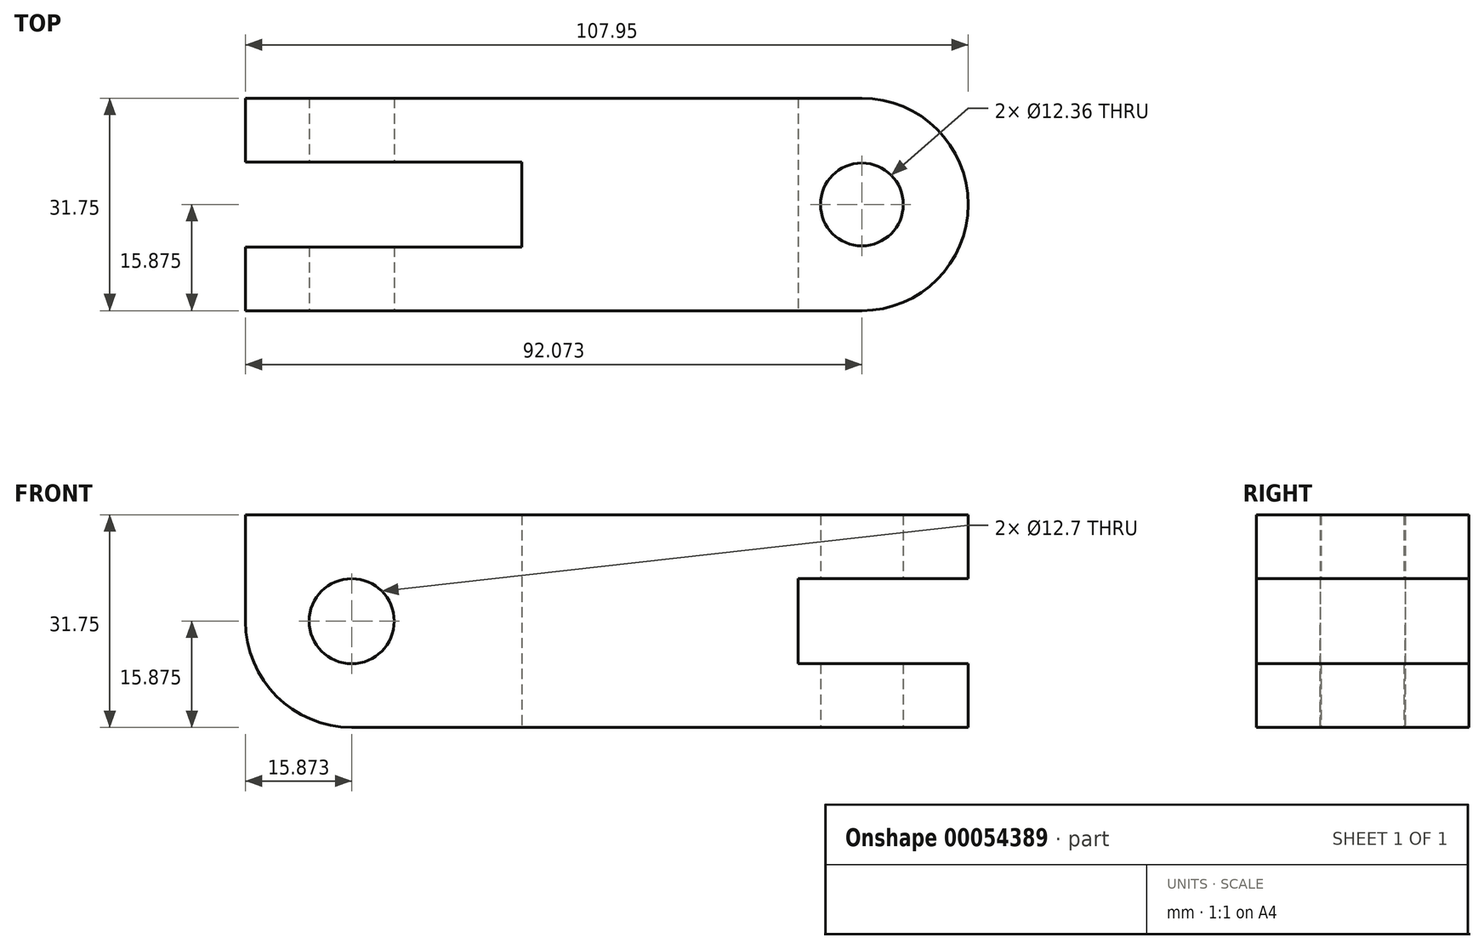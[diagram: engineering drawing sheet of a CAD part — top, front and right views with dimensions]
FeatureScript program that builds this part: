
annotation { "Feature Type Name" : "Feature", "Feature Type Description" : "" }
export const myFeature = defineFeature(function(context is Context, id is Id, definition is map)
    precondition{}
    {
        {
            var Q0;
            Q0=qCreatedBy(makeId("Top.planeOp"),FACE);
            var sketch = newSketch(context, id + "F0", { "sketchPlane" : qUnion([Q0])});
            skLineSegment(sketch, "E0.bottom", {"start": v(-48.28, -15.84) * mm, "end": v(43.8, -15.84) * mm});
            skLineSegment(sketch, "E0.top", {"start": v(-48.28, -47.59) * mm, "end": v(43.8, -47.59) * mm});
            skLineSegment(sketch, "E0.left", {"start": v(-48.28, -15.84) * mm, "end": v(-48.28, -25.36) * mm});
            skLineSegment(sketch, "E1", {"start": v(-48.28, -25.36) * mm, "end": v(-7, -25.36) * mm});
            skLineSegment(sketch, "E2", {"start": v(-48.28, -38.06) * mm, "end": v(-7, -38.06) * mm});
            skLineSegment(sketch, "E3", {"start": v(43.8, -15.84) * mm, "end": v(43.8, -15.84) * mm});
            skLineSegment(sketch, "E4", {"start": v(-7, -25.36) * mm, "end": v(-7, -38.06) * mm});
            skCircle(sketch, "E5", {"center": v(43.8, -31.71) * mm, "radius": 6.18 * mm});
            skArc(sketch, "E6", {"start": v(43.8, -47.59) * mm, "mid": v(59.67, -31.71) * mm, "end": v(43.8, -15.84) * mm});
            skLineSegment(sketch, "E7.trimOffspring", {"start": v(43.8, -47.59) * mm, "end": v(43.8, -47.59) * mm});
            skLineSegment(sketch, "E8.trimOffspring", {"start": v(-48.28, -38.06) * mm, "end": v(-48.28, -47.59) * mm});
            skSolve(sketch);
        }
        {
            var Q0;
            Q0 = qSketchRegion(id + "F0", true);
            extrude(context, id + "F1", {"entities" : qUnion([Q0]), "depth" : 31.75 * mm});
        }
        {
            var Q0;
            Q0=makeQuery(id+"F1.opExtrude","SWEPT_FACE",FACE,{"disambiguationData":[OSD([sQuery(id+"F0.wireOp",EDGE,"E0.top")])]});
            var sketch = newSketch(context, id + "F2", { "sketchPlane" : qUnion([Q0])});
            skLineSegment(sketch, "E9.bottom", {"start": v(-32.4, 31.75) * mm, "end": v(59.67, 31.75) * mm});
            skLineSegment(sketch, "E9.top", {"start": v(-32.4, 0) * mm, "end": v(59.67, 0) * mm});
            skLineSegment(sketch, "E9.right", {"start": v(59.67, 31.75) * mm, "end": v(59.67, 22.23) * mm});
            skLineSegment(sketch, "E10", {"start": v(34.27, 22.23) * mm, "end": v(34.27, 9.52) * mm});
            skArc(sketch, "E11", {"start": v(-32.4, 31.75) * mm, "mid": v(-48.28, 15.87) * mm, "end": v(-32.4, 0) * mm});
            skLineSegment(sketch, "E12", {"start": v(59.67, 22.23) * mm, "end": v(34.27, 22.23) * mm});
            skLineSegment(sketch, "E13", {"start": v(34.27, 9.52) * mm, "end": v(59.67, 9.52) * mm});
            skCircle(sketch, "E14", {"center": v(-32.4, 15.87) * mm, "radius": 6.35 * mm});
            skLineSegment(sketch, "E15.trimOffspring", {"start": v(59.67, 9.52) * mm, "end": v(59.67, 0) * mm});
            skLineSegment(sketch, "E16.bottom", {"start": v(34.27, 22.23) * mm, "end": v(59.67, 22.23) * mm});
            skLineSegment(sketch, "E16.right", {"start": v(59.67, 22.23) * mm, "end": v(59.67, 9.52) * mm});
            skLineSegment(sketch, "E17", {"start": v(-48.28, 31.75) * mm, "end": v(-48.28, 0) * mm});
            skLineSegment(sketch, "E18", {"start": v(-32.4, 31.75) * mm, "end": v(-48.28, 31.75) * mm});
            skLineSegment(sketch, "E19.bottom", {"start": v(-48.28, 31.75) * mm, "end": v(-32.4, 31.75) * mm});
            skLineSegment(sketch, "E19.top", {"start": v(-48.28, 0) * mm, "end": v(-32.4, 0) * mm});
            skLineSegment(sketch, "E19.right", {"start": v(-32.4, 31.75) * mm, "end": v(-32.4, 0) * mm});
            skSolve(sketch);
        }
        {
            var Q0;
            Q0=makeQuery(id+"F2.imprint","IMPRINT",FACE,{"disambiguationData":[TD([[makeQuery(id+"F2.imprint","IMPRINT",EDGE,{"derivedFrom":sQuery(id+"F2.wireOp",EDGE,"E14")}),1.0]])]});
            extrude(context, id + "F3", {"entities" : qUnion([Q0]), "operationType" : NewBodyOperationType.REMOVE, "endBound" : BoundingType.THROUGH_ALL, "oppositeDirection" : true, "depth" : 25.4 * mm});
        }
        {
            var Q0;
            {var subQ0=sQuery(id+"F2.wireOp",EDGE,"E16.right");Q0=makeQuery(id+"F2.imprint","IMPRINT",FACE,{"disambiguationData":[TD([[makeQuery(id+"F2.imprint","IMPRINT",EDGE,{"derivedFrom":subQ0}),-1.0]])]});}
            var Q1;
            {var subQ0=sQuery(id+"F2.wireOp",EDGE,"E10");Q1=makeQuery(id+"F2.imprint","IMPRINT",FACE,{"disambiguationData":[TD([[makeQuery(id+"F2.imprint","IMPRINT",EDGE,{"derivedFrom":subQ0}),1.0]])]});}
            extrude(context, id + "F4", {"entities" : qUnion([Q0, Q1]), "operationType" : NewBodyOperationType.REMOVE, "endBound" : BoundingType.THROUGH_ALL, "oppositeDirection" : true, "depth" : 25.4 * mm});
        }
        {
            var Q0;
            {var subQ0=sQuery(id+"F2.wireOp",EDGE,"E19.bottom");Q0=makeQuery(id+"F2.imprint","IMPRINT",FACE,{"disambiguationData":[TD([[makeQuery(id+"F2.imprint","IMPRINT",EDGE,{"derivedFrom":subQ0}),-1.0]])]});}
            var Q1;
            {var subQ0=sQuery(id+"F2.wireOp",EDGE,"E19.top");Q1=makeQuery(id+"F2.imprint","IMPRINT",FACE,{"disambiguationData":[TD([[makeQuery(id+"F2.imprint","IMPRINT",EDGE,{"derivedFrom":subQ0}),1.0]])]});}
            extrude(context, id + "F5", {"entities" : qUnion([Q0, Q1]), "operationType" : NewBodyOperationType.REMOVE, "endBound" : BoundingType.THROUGH_ALL, "oppositeDirection" : true, "depth" : 25.4 * mm});
        }
    });
